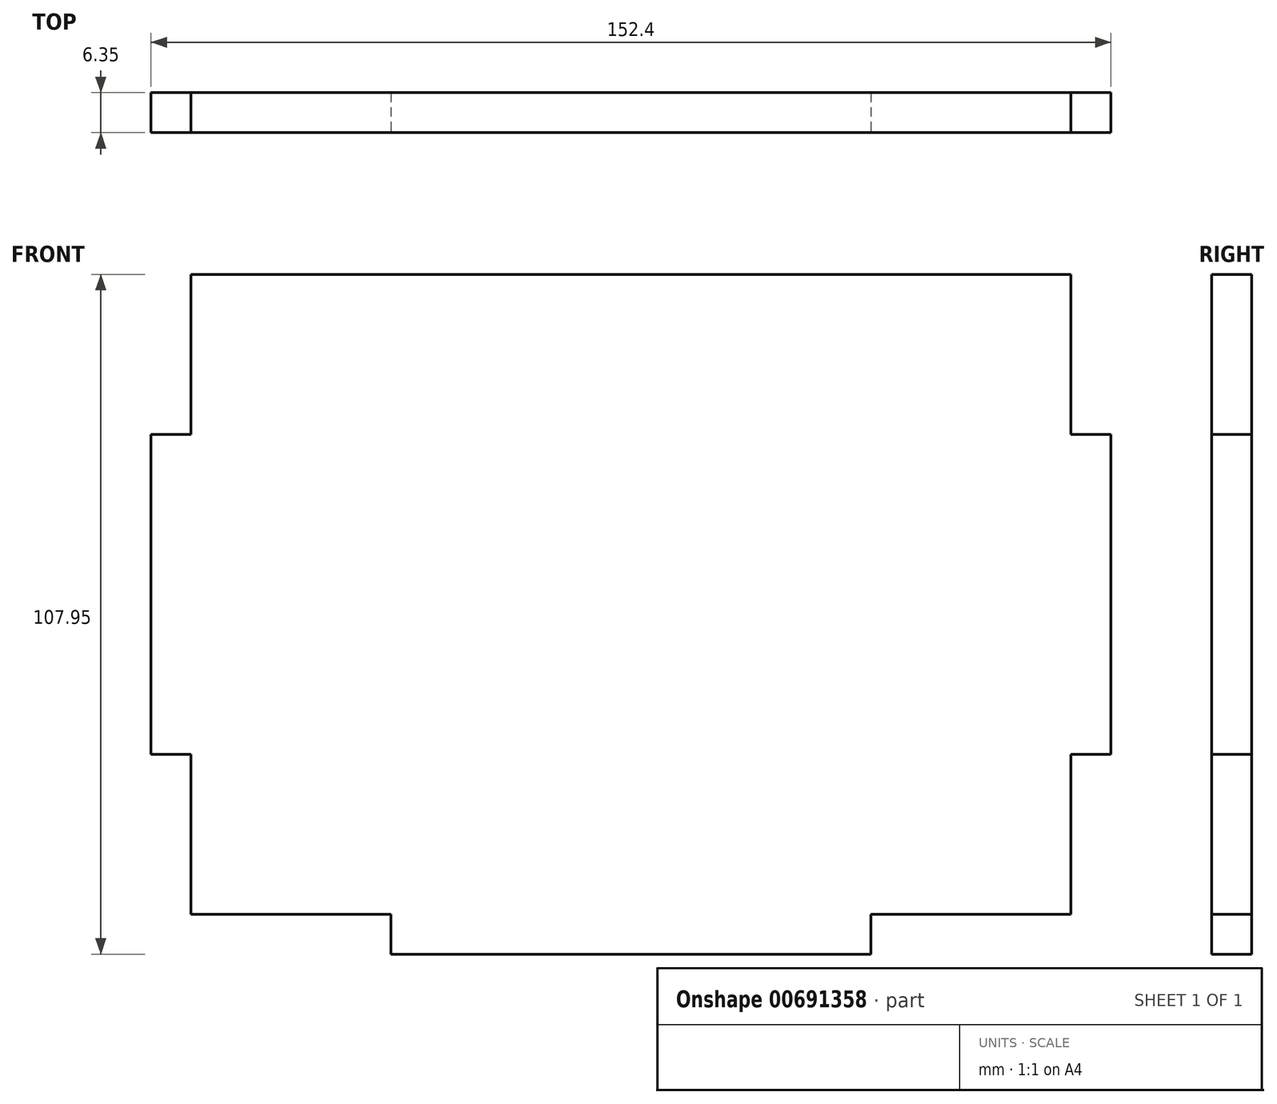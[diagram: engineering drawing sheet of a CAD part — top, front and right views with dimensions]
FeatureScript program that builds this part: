
annotation { "Feature Type Name" : "Feature", "Feature Type Description" : "" }
export const myFeature = defineFeature(function(context is Context, id is Id, definition is map)
    precondition{}
    {
        {
            var Q0;
            Q0=qCreatedBy(makeId("Front.planeOp"),FACE);
            var sketch = newSketch(context, id + "F0", { "sketchPlane" : qUnion([Q0])});
            skLineSegment(sketch, "E0.bottom", {"start": v(-69.85, 101.6) * mm, "end": v(69.85, 101.6) * mm});
            skLineSegment(sketch, "E0.top", {"start": v(-69.85, 0) * mm, "end": v(69.85, 0) * mm});
            skLineSegment(sketch, "E0.left", {"start": v(-69.85, 101.6) * mm, "end": v(-69.85, 0) * mm});
            skLineSegment(sketch, "E0.right", {"start": v(69.85, 101.6) * mm, "end": v(69.85, 0) * mm});
            skSolve(sketch);
        }
        {
            var Q0;
            Q0=qSketchRegion(id+"F0",true);
            extrude(context, id + "F1", {"entities" : qUnion([Q0]), "depth" : 6.35 * mm, "offsetDistance" : 25.4 * mm});
        }
        {
            var Q0;
            Q0=makeQuery(id+"F1.opExtrude","CAP_FACE",FACE,{"disambiguationData":[OSD([sQuery(id+"F0.wireOp",EDGE,"E0.bottom"),sQuery(id+"F0.wireOp",EDGE,"E0.top"),sQuery(id+"F0.wireOp",EDGE,"E0.left"),sQuery(id+"F0.wireOp",EDGE,"E0.right")])],"isStart":false});
            var sketch = newSketch(context, id + "F2", { "sketchPlane" : qUnion([Q0])});
            skLineSegment(sketch, "E1.bottom", {"start": v(-38.1, 0) * mm, "end": v(38.1, 0) * mm});
            skLineSegment(sketch, "E1.top", {"start": v(-38.1, -6.35) * mm, "end": v(38.1, -6.35) * mm});
            skLineSegment(sketch, "E1.left", {"start": v(-38.1, 0) * mm, "end": v(-38.1, -6.35) * mm});
            skLineSegment(sketch, "E1.right", {"start": v(38.1, 0) * mm, "end": v(38.1, -6.35) * mm});
            skSolve(sketch);
        }
        {
            var Q0;
            Q0=qSketchRegion(id+"F2",true);
            extrude(context, id + "F3", {"entities" : qUnion([Q0]), "operationType" : NewBodyOperationType.ADD, "oppositeDirection" : true, "depth" : 6.35 * mm, "offsetDistance" : 25.4 * mm});
        }
        {
            var Q0;
            Q0=makeQuery(id+"F3.boolean.opBoolean","MERGE",FACE,{"derivedFrom":[makeQuery(id+"F1.opExtrude","CAP_FACE",FACE,{"disambiguationData":[OSD([sQuery(id+"F0.wireOp",EDGE,"E0.bottom"),sQuery(id+"F0.wireOp",EDGE,"E0.top"),sQuery(id+"F0.wireOp",EDGE,"E0.left"),sQuery(id+"F0.wireOp",EDGE,"E0.right")])],"isStart":false}),makeQuery(id+"F3.opExtrude","CAP_FACE",FACE,{"disambiguationData":[OSD([sQuery(id+"F2.wireOp",EDGE,"E1.bottom"),sQuery(id+"F2.wireOp",EDGE,"E1.top"),sQuery(id+"F2.wireOp",EDGE,"E1.left"),sQuery(id+"F2.wireOp",EDGE,"E1.right")])],"isStart":true})]});
            var sketch = newSketch(context, id + "F4", { "sketchPlane" : qUnion([Q0])});
            skLineSegment(sketch, "E2.bottom", {"start": v(-69.85, 76.2) * mm, "end": v(-76.2, 76.2) * mm});
            skLineSegment(sketch, "E2.top", {"start": v(-69.85, 25.4) * mm, "end": v(-76.2, 25.4) * mm});
            skLineSegment(sketch, "E2.left", {"start": v(-69.85, 76.2) * mm, "end": v(-69.85, 25.4) * mm});
            skLineSegment(sketch, "E2.right", {"start": v(-76.2, 76.2) * mm, "end": v(-76.2, 25.4) * mm});
            skLineSegment(sketch, "E3.MirrorCS", {"start": v(76.2, 76.2) * mm, "end": v(76.2, 25.4) * mm});
            skLineSegment(sketch, "E4.MirrorCS", {"start": v(69.85, 76.2) * mm, "end": v(69.85, 25.4) * mm});
            skLineSegment(sketch, "E5.MirrorCS", {"start": v(69.85, 76.2) * mm, "end": v(76.2, 76.2) * mm});
            skLineSegment(sketch, "E6.MirrorCS", {"start": v(69.85, 25.4) * mm, "end": v(76.2, 25.4) * mm});
            skSolve(sketch);
        }
        {
            var Q0;
            Q0=qSketchRegion(id+"F4",true);
            extrude(context, id + "F5", {"entities" : qUnion([Q0]), "operationType" : NewBodyOperationType.ADD, "oppositeDirection" : true, "depth" : 6.35 * mm, "offsetDistance" : 25.4 * mm});
        }
    });
